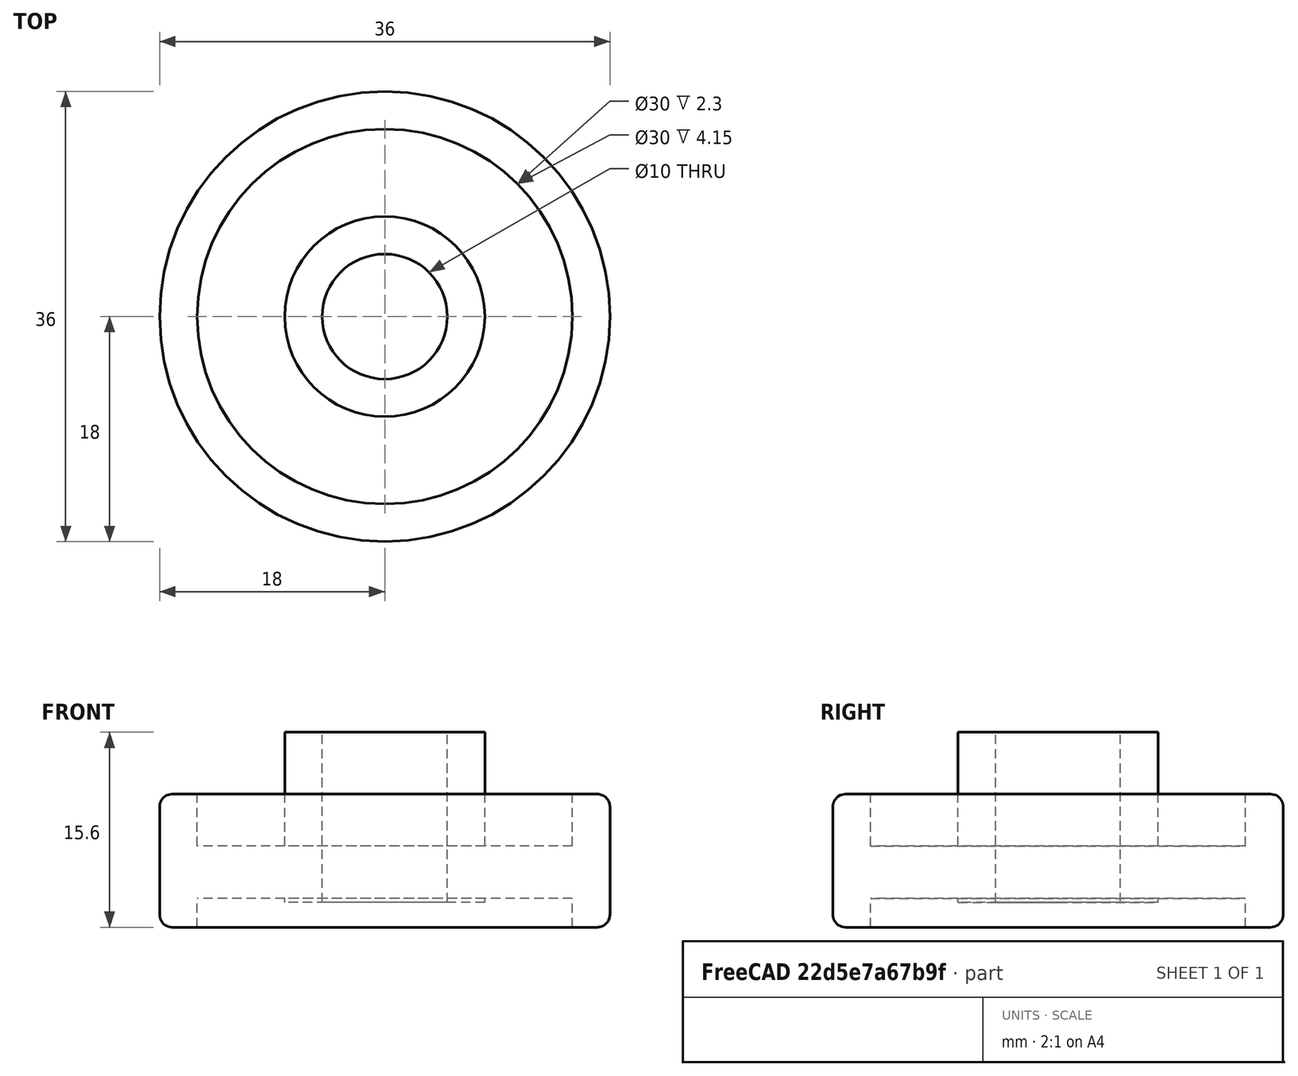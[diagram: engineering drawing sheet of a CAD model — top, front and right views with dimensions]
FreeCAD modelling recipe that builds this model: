
FCSTD DOCUMENT  (FreeCAD 0.18.4R)
Label: lavastoviglie
License: All rights reserved
LicenseURL: http://en.wikipedia.org/wiki/All_rights_reserved
objects: Part::Cylinder×5, Part::Cut×3, PartDesign::Fillet×2, Part::MultiFuse×1, PartDesign::FeatureBase×1, PartDesign::Body×1
note: 13 computed .brp shape members not serialized (recipe doc carries the construction recipe); baked Part::Feature solids carry a one-line shape summary decoded from their .brp

FEATURE [Part::Cylinder] Cylinder
  Angle = 360
  AttacherType = Attacher::AttachEngine3D
  Height = 10.65
  Radius = 18
FEATURE [Part::Cylinder] Cylinder001
  Angle = 360
  AttacherType = Attacher::AttachEngine3D
  Height = 4.5
  Placement = pos=(0,0,6.5) rot=(0,0,1;0rad)
  Radius = 15
FEATURE [Part::Cylinder] Cylinder002
  Angle = 360
  AttacherType = Attacher::AttachEngine3D
  Height = 2.8
  Placement = pos=(0,0,-0.5) rot=(0,0,1;0rad)
  Radius = 15
FEATURE [Part::Cut] Cut
  Base = -> Cylinder
  Tool = -> Cylinder001
FEATURE [Part::Cut] Cut001
  Base = -> Cut
  Tool = -> Cylinder002
FEATURE [Part::Cylinder] Cylinder003
  Angle = 360
  AttacherType = Attacher::AttachEngine3D
  Height = 13.6
  Placement = pos=(0,0,2) rot=(0,0,1;0rad)
  Radius = 8
FEATURE [Part::Cylinder] Cylinder004
  Angle = 360
  AttacherType = Attacher::AttachEngine3D
  Height = 25.6
  Placement = pos=(0,0,-1) rot=(0,0,1;0rad)
  Radius = 5
FEATURE [Part::MultiFuse] Fusion
  Shapes = -> [Cylinder003,Cut001]
FEATURE [Part::Cut] Cut002
  Base = -> Fusion
  Tool = -> Cylinder004
FEATURE [PartDesign::FeatureBase] BaseFeature
  BaseFeature = -> Cut002
FEATURE [PartDesign::Fillet] Fillet
  Base = -> BaseFeature [Edge10]
  BaseFeature = -> BaseFeature
  Radius = 1
FEATURE [PartDesign::Fillet] Fillet001
  Base = -> Fillet [Edge8]
  BaseFeature = -> Fillet
  Radius = 1
FEATURE [PartDesign::Body] Body
  BaseFeature = -> Cut002
  Group = -> [BaseFeature,Fillet,Fillet001]
  Origin = -> Origin
  Tip = -> Fillet001
